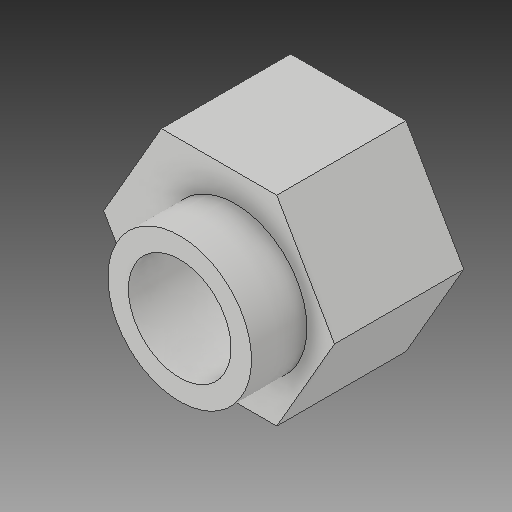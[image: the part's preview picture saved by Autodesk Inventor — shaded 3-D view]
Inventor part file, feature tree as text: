
AUTODESK INVENTOR PART (.ipt)
format: ipt  version: 2018 (Build 220112000, 112)  size: 121,344 bytes
history: native  units: mm
features: other x3, sketch x3
ambient origin geometry x8: Origin, YZ Plane, XZ Plane, XY Plane, X Axis, Y Axis, Z Axis, Center Point
bodies: Solid1 (feature_tree)
feature tree (6):
  other  "Eccentric Spacer_MIR1.ipt"
  other  "Solid1::Eccentric Spacer_MIR1.ipt"
  other  "TaggingFeature1"
  sketch  "Sketch1"  dims[d0=10.0mm]
  sketch  "Sketch2"
  sketch  "Sketch3"
